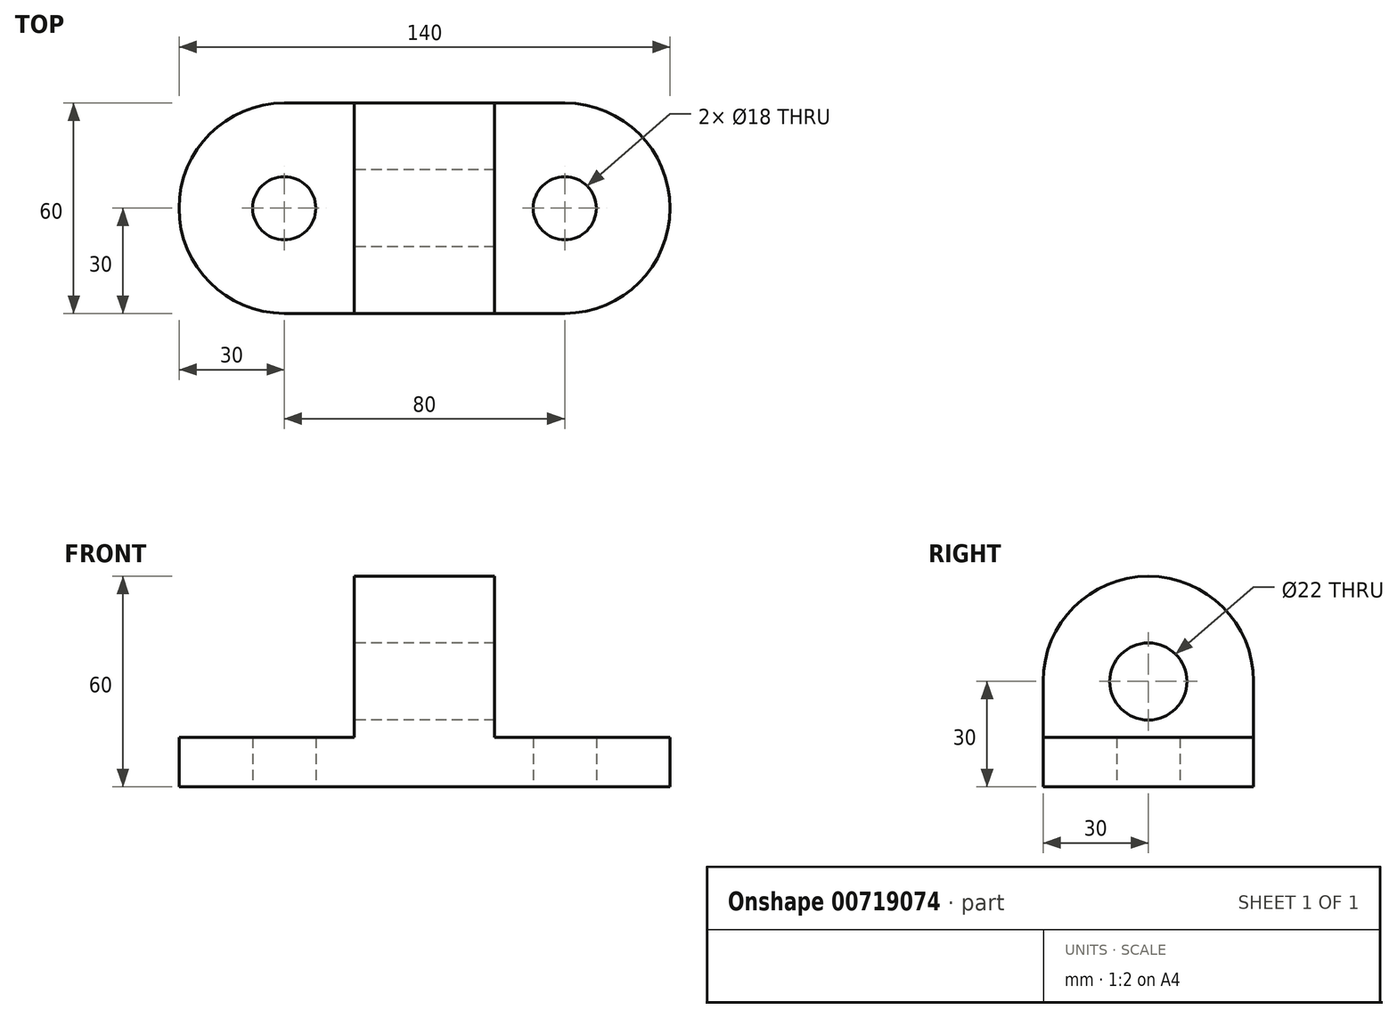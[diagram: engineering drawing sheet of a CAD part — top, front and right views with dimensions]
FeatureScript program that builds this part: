
annotation { "Feature Type Name" : "Feature", "Feature Type Description" : "" }
export const myFeature = defineFeature(function(context is Context, id is Id, definition is map)
    precondition{}
    {
        {
            var Q0;
            Q0=qCreatedBy(makeId("Top.planeOp"),FACE);
            var sketch = newSketch(context, id + "F0", { "sketchPlane" : qUnion([Q0])});
            skLineSegment(sketch, "E0.bottom", {"start": v(-40, 30) * mm, "end": v(40, 30) * mm});
            skLineSegment(sketch, "E0.top", {"start": v(-40, -30) * mm, "end": v(40, -30) * mm});
            skPoint(sketch, "E0.middle", {"position": v(0, 0) * mm});
            skLineSegment(sketch, "E1", {"start": v(-40, 30) * mm, "end": v(-40, -30) * mm, "construction": true});
            skLineSegment(sketch, "E2", {"start": v(40, 30) * mm, "end": v(40, -30) * mm, "construction": true});
            skArc(sketch, "E3", {"start": v(40, -30) * mm, "mid": v(70, 0) * mm, "end": v(40, 30) * mm});
            skArc(sketch, "E4", {"start": v(-40, 30) * mm, "mid": v(-70, 0) * mm, "end": v(-40, -30) * mm});
            skCircle(sketch, "E5", {"center": v(-40, 0) * mm, "radius": 9 * mm});
            skCircle(sketch, "E6", {"center": v(40, 0) * mm, "radius": 9 * mm});
            skPoint(sketch, "E7.orphan", {"position": v(-70, 30) * mm});
            skPoint(sketch, "E8.orphan", {"position": v(-70, -30) * mm});
            skPoint(sketch, "E0.right.end.orphan", {"position": v(70, -30) * mm});
            skPoint(sketch, "E9.orphan", {"position": v(70, 30) * mm});
            skSolve(sketch);
        }
        {
            var Q0;
            Q0=makeQuery(id+"F0.imprint","IMPRINT",FACE,{"disambiguationData":[TD([[makeQuery(id+"F0.imprint","IMPRINT",EDGE,{"derivedFrom":sQuery(id+"F0.wireOp",EDGE,"E0.bottom")}),-1.0]])]});
            extrude(context, id + "F1", {"entities" : qUnion([Q0]), "depth" : 14 * mm, "offsetDistance" : 25 * mm});
        }
        {
            var Q0;
            Q0=qCreatedBy(makeId("Right.planeOp"),FACE);
            var sketch = newSketch(context, id + "F2", { "sketchPlane" : qUnion([Q0])});
            skLineSegment(sketch, "E10", {"start": v(0, 0) * mm, "end": v(0, 45.73) * mm, "construction": true});
            skLineSegment(sketch, "E11", {"start": v(11.82, 30) * mm, "end": v(-13.25, 30) * mm, "construction": true});
            skArc(sketch, "E12", {"start": v(30, 30) * mm, "mid": v(0, 60) * mm, "end": v(-30, 30) * mm});
            skLineSegment(sketch, "E13", {"start": v(30, 30) * mm, "end": v(30, 13.78) * mm});
            skLineSegment(sketch, "E14", {"start": v(-30, 30) * mm, "end": v(-30, 13.87) * mm});
            skLineSegment(sketch, "E15", {"start": v(30, 13.78) * mm, "end": v(-30, 13.87) * mm});
            skCircle(sketch, "E16", {"center": v(0, 30) * mm, "radius": 11 * mm});
            skSolve(sketch);
        }
        {
            var Q0;
            Q0=makeQuery(id+"F2.imprint","IMPRINT",FACE,{"disambiguationData":[TD([[makeQuery(id+"F2.imprint","IMPRINT",EDGE,{"derivedFrom":sQuery(id+"F2.wireOp",EDGE,"E12")}),1.0]])]});
            extrude(context, id + "F3", {"entities" : qUnion([Q0]), "operationType" : NewBodyOperationType.ADD, "depth" : 20 * mm, "offsetDistance" : 25 * mm, "hasSecondDirection" : true, "secondDirectionOppositeDirection" : true, "secondDirectionDepth" : 20 * mm});
        }
    });
